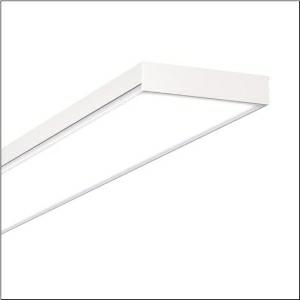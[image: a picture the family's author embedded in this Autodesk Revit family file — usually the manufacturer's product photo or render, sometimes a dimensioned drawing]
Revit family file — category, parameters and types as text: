
# Revit family: apollon_r__31_surface_51mp25wm2441wa_3dc9
name_source: partatom
category: Lighting Fixtures
units: mm (PartAtom-declared; Revit-internal decimal feet)

## family parameters
Cut with Voids When Loaded = No
Host = Face
Light Source = No
Part Type = Normal
Room Calculation Point = No
Round Connector Dimension = Use Diameter
Shared = No

## types (1)
- Apollon® 31 Surface (1 x LED, 3800 lm, 27 W, 4000K)
    Apparent Load = 27 VA
    CIE Flux Codes = 61 87 97 97 100
    Color Rendering = 80
    Color Temperature = 4000K
    Default Elevation = 1800 mm
    Description = Apollon® 31 Surface, office luminaire, primary optical cover: micro prismatic cover, of PMMA, light emission: direct distribution, primary light characteristic: symmetric, installation type: surface-mounted, LED, rated luminous flux: 3.800lm, luminous efficacy: 139lm/W, light colour: 840, colour temperature: 4000K, control gear: ON/OFF Multilumen, with terminal, 3-pole, mains connection: 220..240V, AC, 50/60Hz, rated input power: 27W, housing, of sheet steel, coil coated, traffic white (RAL 9016), length: 1.245mm, width: 200mm, height: 44mm, protection rating (complete): IP20, insulation class (complete): insulation class II (safety insulation), certification: CE, impact resistance: IK02, permissible operating ambient temperature: -20..+40°C, packaging unit: 1 piece
    Height = 44 mm
    Lamp = 1 x LED
    Lamp Light Flux = 3800 lm
    Lamp Power = 27 W
    Lamp count = 1
    Length = 1245 mm
    Luminous efficacy = 141 lm/W
    Manufacturer = Siteco
    ModVariant = No
    Model = 51MP25WM2441WA
    Mounting Place = Ceiling
    Mounting Type = Surface mounted
    Number of Poles = 1
    OnlyDefault = Yes
    Power Factor = 1
    Product Name = Apollon® 31 Surface
    Product group = office luminaire | ceiling mounted
    ProductGroupID = 302
    Protection Class = Protection class II
    Protection Degree = IP 20
    RLX_Detail_Level = 1
    RLX_Emergency_Light_Flux = 0 lm
    RLX_Emergency_Type = 0
    RLX_Emergency_Type_DB = No
    RlxData = <blob elided: 20761 chars, md5=224b16c1>
    Socket = socket
    Standby Power = 0 W
    System Light Flux = 3800 lm
    System Power = 27 W
    Type Comments = Product without accessories
    Type Image = l_1313658.jpg
    URL = http://relux.com
    VarID = ---
    Voltage = 0 V
    Weight = 0.00 kg
    Width = 200 mm  [stored 0.656168 ft]

note: [stored X ft] marks values corroborated as IEEE doubles in the binary element streams (Revit-internal decimal feet)

## geometry (parser evidence)
native form markers: Blend x4, Sweep x12
no freeform markers — native parametric forms only
